# Revit family: eg-50_60etxc2_ftxc2-fq_50Hz
name_source: partatom
category: 機械設備
units: mm (PartAtom-declared; Revit-internal decimal feet)

## family parameters
OmniClass タイトル = Industrial Ventilating Equipment
OmniClass 番号 = 23.75.35.21.17
パーツ タイプ = 標準
ロード時にボイドで切り取り = はい
丸型コネクタ寸法 = 直径を使用
作業面ベース = いいえ
共有 = いいえ
常に垂直 = はい
部屋計算ポイント = はい

## types (4) — shared parameters
IfcExportAs = IfcFanType
IfcExportType = TUBEAXIAL
MID風量 = 0.0 m³/h
MIN風量 = 0.0 m³/h
OmniClassCode = 23-33 31 19 11 17
URL = https://www.mitsubishielectric.co.jp
Uniclass2015Code = Pr_65_67_29_67
Uniclass2015Title = Propeller fans
Uniclass2015Version = Systems v1.9
オリフィス_Depth = 70  [stored 0.229659 ft]
ファンの種類 = 軸流羽根
フレームの厚さ = 142  [stored 0.465879 ft]
モーター径 = 164  [stored 0.538058 ft]
レグ_Height = 413  [stored 1.35499 ft]
レグ_Width = 413  [stored 1.35499 ft]
仕様書バージョン = Version1.0
企業コード = 108420
分類コード = 50052503100110
周波数 = 50 Hz
呼称 = 有圧扇
極 = 6
極数 = 3
法定耐用年数 = 15
相 = 3
製品リリース年月 = 2022年6月1日
製品出荷対象 = 国内
製造元 = 三菱電機株式会社
設置方法 = 壁付
説明 = 産業用有圧換気扇 低騒音形ステンレスタイプ オールステンレス高耐食タイプ 給気専用
負荷分類 = 3_ファン類
運転質量 = 0.00 kg

## per-type parameters (varying)
| type | Depth | Height | MAX風量 | Width | オリフィス径 | モデル | レグ_Depth | 価格 | 消費電力 | 羽根径 | 製品質量 | 質量 | 電動機出力 | 電圧 |
| EG-50ETXC2-FQ_200V | 340  [stored 1.11549 ft] | 620  [stored 2.03412 ft] | 6060.0 m³/h | 620  [stored 2.03412 ft] | 605  [stored 1.98491 ft] | EG-50ETXC2-FQ | 304 | 883000 $ | 223 W | ∅500 | 30.00 kg | 36.00 kg | 400 W | 200 V |
| EG-60FTXC2-FQ_200V | 358  [stored 1.17454 ft] | 710 | 9420.0 m³/h | 710 | 705  [stored 2.31299 ft] | EG-60FTXC2-FQ | 322 | 1164000 $ | 370 W | ∅600 | 34.00 kg | 40.80 kg | 750 W | 200 V |
| EG-50ETXC2-FQ_220V | 340  [stored 1.11549 ft] | 620  [stored 2.03412 ft] | 6060.0 m³/h | 620  [stored 2.03412 ft] | 605  [stored 1.98491 ft] | EG-50ETXC2-FQ | 304 | 883000 $ | 235 W | ∅500 | 30.00 kg | 36.00 kg | 400 W | 220 V |
| EG-60FTXC2-FQ_220V | 358  [stored 1.17454 ft] | 710 | 9420.0 m³/h | 710 | 705  [stored 2.31299 ft] | EG-60FTXC2-FQ | 322 | 1164000 $ | 395 W | ∅600 | 34.00 kg | 40.80 kg | 750 W | 220 V |

note: [stored X ft] marks values corroborated as IEEE doubles in the binary element streams (Revit-internal decimal feet)
